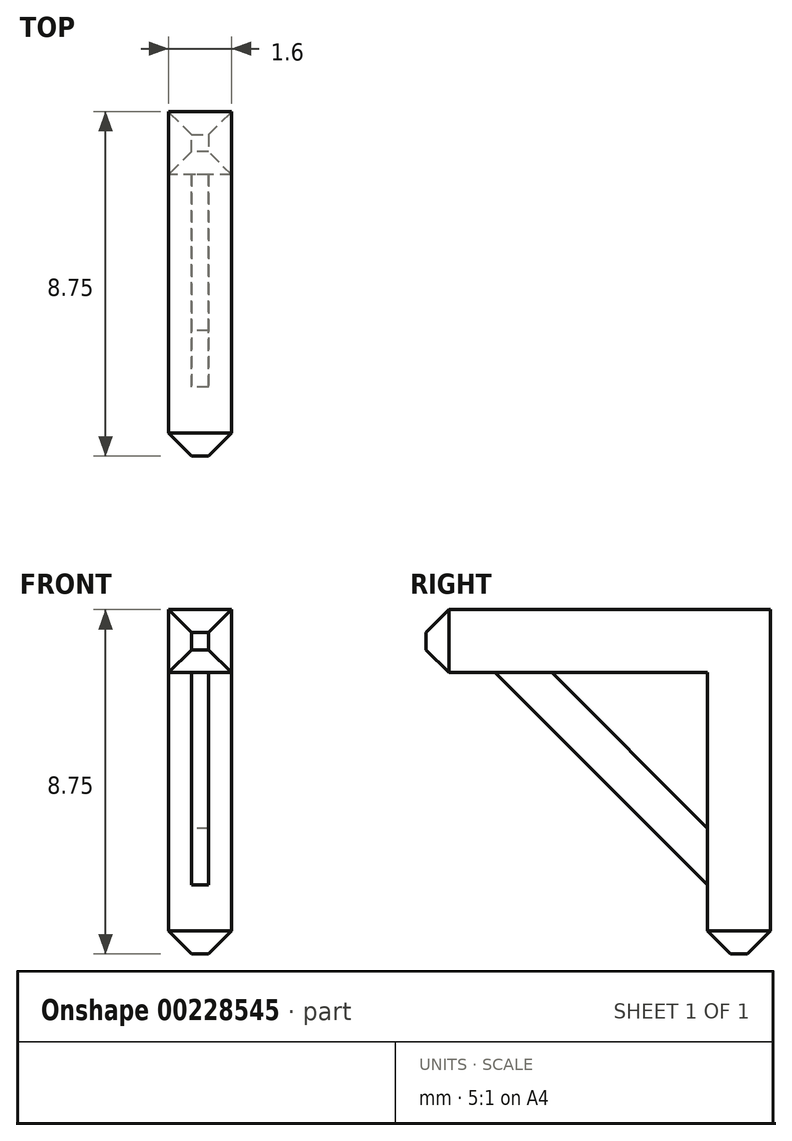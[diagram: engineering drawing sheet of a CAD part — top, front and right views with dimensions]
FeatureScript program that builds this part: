
annotation { "Feature Type Name" : "Feature", "Feature Type Description" : "" }
export const myFeature = defineFeature(function(context is Context, id is Id, definition is map)
    precondition{}
    {
        {
            var Q0;
            Q0=qCreatedBy(makeId("Right.planeOp"),FACE);
            var sketch = newSketch(context, id + "F0", { "sketchPlane" : qUnion([Q0])});
            skLineSegment(sketch, "E0", {"start": v(-762, 0) * mm, "end": v(0, 0) * mm});
            skLineSegment(sketch, "E1", {"start": v(0, 0) * mm, "end": v(0, -762) * mm});
            skLineSegment(sketch, "E2", {"start": v(0, -762) * mm, "end": v(-139.7, -762) * mm});
            skLineSegment(sketch, "E3", {"start": v(-139.7, -762) * mm, "end": v(-139.7, -139.7) * mm});
            skLineSegment(sketch, "E4", {"start": v(-139.7, -139.7) * mm, "end": v(-762, -139.7) * mm});
            skLineSegment(sketch, "E5", {"start": v(-762, 0) * mm, "end": v(-762, -139.7) * mm});
            skSolve(sketch);
        }
        {
            var Q0;
            Q0=makeQuery(id+"F0.imprint","IMPRINT",FACE,{"disambiguationData":[TD([[makeQuery(id+"F0.imprint","IMPRINT",EDGE,{"derivedFrom":sQuery(id+"F0.wireOp",EDGE,"E0")}),-1.0]])]});
            extrude(context, id + "F1", {"entities" : qUnion([Q0]), "endBound" : BoundingType.SYMMETRIC, "depth" : 139.7 * mm});
        }
        {
            var Q0;
            Q0=makeQuery(id+"F1.opExtrude","SWEPT_EDGE",EDGE,{"disambiguationData":[OSD([sQuery(id+"F0.wireOp",EDGE,"E4"),sQuery(id+"F0.wireOp",EDGE,"E5")])]});
            var Q1;
            Q1=makeQuery(id+"F1.opExtrude","CAP_EDGE",EDGE,{"disambiguationData":[OSD([sQuery(id+"F0.wireOp",EDGE,"E2")])],"isStart":false});
            var Q2;
            Q2=makeQuery(id+"F1.opExtrude","SWEPT_EDGE",EDGE,{"disambiguationData":[OSD([sQuery(id+"F0.wireOp",EDGE,"E2"),sQuery(id+"F0.wireOp",EDGE,"E3")])]});
            var Q3;
            Q3=makeQuery(id+"F1.opExtrude","CAP_EDGE",EDGE,{"disambiguationData":[OSD([sQuery(id+"F0.wireOp",EDGE,"E2")])],"isStart":true});
            var Q4;
            Q4=makeQuery(id+"F1.opExtrude","SWEPT_EDGE",EDGE,{"disambiguationData":[OSD([sQuery(id+"F0.wireOp",EDGE,"E1"),sQuery(id+"F0.wireOp",EDGE,"E2")])]});
            var Q5;
            Q5=makeQuery(id+"F1.opExtrude","CAP_EDGE",EDGE,{"disambiguationData":[OSD([sQuery(id+"F0.wireOp",EDGE,"E5")])],"isStart":true});
            var Q6;
            Q6=makeQuery(id+"F1.opExtrude","SWEPT_EDGE",EDGE,{"disambiguationData":[OSD([sQuery(id+"F0.wireOp",EDGE,"E0"),sQuery(id+"F0.wireOp",EDGE,"E5")])]});
            var Q7;
            Q7=makeQuery(id+"F1.opExtrude","CAP_EDGE",EDGE,{"disambiguationData":[OSD([sQuery(id+"F0.wireOp",EDGE,"E5")])],"isStart":false});
            chamfer(context, id + "F2", {"entities" : qUnion([Q0, Q1, Q2, Q3, Q4, Q5, Q6, Q7]), "chamferType" : ChamferType.TWO_OFFSETS, "width1" : 50.8 * mm, "oppositeDirection" : false, "width2" : 50.8 * mm, "tangentPropagation" : true});
        }
        {
            var Q0;
            Q0=qCreatedBy(makeId("Right.planeOp"),FACE);
            var sketch = newSketch(context, id + "F3", { "sketchPlane" : qUnion([Q0])});
            skLineSegment(sketch, "E6", {"start": v(-609.6, -139.7) * mm, "end": v(-483.88, -139.7) * mm});
            skLineSegment(sketch, "E7", {"start": v(-483.88, -139.7) * mm, "end": v(-139.7, -483.88) * mm});
            skLineSegment(sketch, "E8", {"start": v(-139.7, -483.88) * mm, "end": v(-139.7, -609.6) * mm});
            skLineSegment(sketch, "E9", {"start": v(-139.7, -609.6) * mm, "end": v(-609.6, -139.7) * mm});
            skSolve(sketch);
        }
        {
            var Q0;
            Q0=makeQuery(id+"F3.imprint","IMPRINT",FACE,{"disambiguationData":[TD([[makeQuery(id+"F3.imprint","IMPRINT",EDGE,{"derivedFrom":sQuery(id+"F3.wireOp",EDGE,"E6")}),-1.0]])]});
            extrude(context, id + "F4", {"entities" : qUnion([Q0]), "operationType" : NewBodyOperationType.ADD, "endBound" : BoundingType.SYMMETRIC, "depth" : 38.1 * mm});
        }
        {
            var Q0;
            Q0=makeQuery(id+"F1.opExtrude","SWEPT_BODY",BODY,{"disambiguationData":[OSD([sQuery(id+"F0.wireOp",EDGE,"E0"),sQuery(id+"F0.wireOp",EDGE,"E1"),sQuery(id+"F0.wireOp",EDGE,"E2"),sQuery(id+"F0.wireOp",EDGE,"E3"),sQuery(id+"F0.wireOp",EDGE,"E4"),sQuery(id+"F0.wireOp",EDGE,"E5")])]});
            var Q1;
            Q1=qCreatedBy(makeId("Origin.pointOp"),VERTEX);
            transform(context, id + "F5", {"entities" : qUnion([Q0]), "transformType" : TransformType.SCALE_UNIFORMLY, "scale" : 1 / 87.1, "scalePoint" : qUnion([Q1]), "makeCopy" : false});
        }
    });
